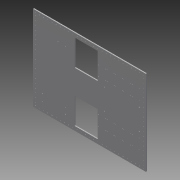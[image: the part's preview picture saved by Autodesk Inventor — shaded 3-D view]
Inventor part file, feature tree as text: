
AUTODESK INVENTOR PART (.ipt)
format: ipt  version: 2014 SP1 (Build 180222100, 222)  size: 260,096 bytes
history: native  units: in
note: dims shown in document units (in); Inventor stores cm internally (conversion verified against a paired STEP export)
features: extrude x1, sketch x1
ambient origin geometry x8: Origin, YZ Plane, XZ Plane, XY Plane, X Axis, Y Axis, Z Axis, Center Point
bodies: Solid1 (feature_tree)
feature tree (2):
  extrude  "Extrusion1"  [1 undecoded]
  sketch  "Sketch1"  dims[d0=0.25in d1=0.0in]
note: 1 required parameter value undecoded (feature->parameter linkage not recoverable at this tier; creation-order binding heuristic only, values carry confidence <= 0.55)
